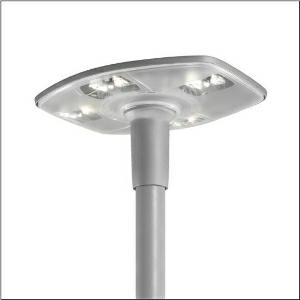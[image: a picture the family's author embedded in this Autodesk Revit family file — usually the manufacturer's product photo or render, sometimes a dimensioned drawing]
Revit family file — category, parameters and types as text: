
# Revit family: dl_r__30_led___st1_2c_5xa513271b08a5_992b
name_source: partatom
category: Lighting Fixtures
units: mm (PartAtom-declared; Revit-internal decimal feet)

## family parameters
Cut with Voids When Loaded = No
Host = Face
Light Source = No
Part Type = Normal
Room Calculation Point = No
Round Connector Dimension = Use Diameter
Shared = No

## types (1)
- --- (1 x LED, 5540 lm, 48.9 W, 4000K)
    Apparent Load = 49 VA
    CIE Flux Codes = 32 71 98 100 100
    Color Rendering = 70
    Color Temperature = 4000K
    Default Elevation = 1800 mm
    Description = DL® 30 LED, mast luminaire, primary light control with 3 zone facetted reflector, of plastic, aluminium vaporised, highly specular, primary optical cover: cover, of PMMA, structured, transparent, light distribution: ST1.2c, light emission: direct distribution, primary light characteristic: asymmetric, crossroads, installation type: post-top, LED High Power LED, rated luminous flux: 5.540 lm, light colour: 740, colour temperature: 4000K, control gear: ECG Plus, control: flexible luminous flux parameterisation, time-dependent luminous flux control, constant luminous flux control, digital communication interface, power reduction, electronic power reduction, mains connection: 220..240V, AC, 50/60Hz, start of lifetime: 49 W, end of lifetime: 51 W, reduction: 23 W, luminaire housing, of diecast aluminium, powder-coated, Siteco® metallic grey (DB 702S), length: 600 mm, width: 510 mm, height: 290mm, spigot size: d x l = 76 x 100mm (post-top) | with reducer (optional accessory) 60 x 100mm, protection rating (complete): IP66, insulation class (complete): insulation class II (safety insulation), certification: CE, ENEC, VDE, impact resistance: IK08, permissible ambient temperature for indoor applications: -25..+30°C, standard-compliant lighting for roads and squares, packaging unit: 1 piece

Light Distribution: ST1.2c
    Height = 290 mm
    Lamp = 1 x LED
    Lamp Light Flux = 5540 lm
    Lamp Power = 48.9 W
    Lamp count = 1
    Length = 510 mm
    Luminous efficacy = 113 lm/W
    Manufacturer = Siteco
    ModVariant = No
    Model = 5XA513271B08A5
    Number of Poles = 1
    OnlyDefault = Yes
    Power Factor = 1
    Product Name = DL® 30 LED | ST1.2c
    Product group = mast luminaire | pylon top
    ProductGroupID = 6100
    Protection Class = Protection class II
    Protection Degree = IP 66
    RLX_Detail_Level = 1
    RlxData = <blob elided: 86577 chars, md5=b1d05cf7>
    Socket = socket
    Standby Power = 0 W
    System Light Flux = 5540 lm
    System Power = 49 W
    Type Comments = factory setting: luminous flux: 100 % | dim-lin: 254 | 497 mA
    Type Image = l_1006003.jpg
    URL = http://relux.com
    VarID = @adj_130929
    Voltage = 0 V
    Weight = 0.00 kg
    Width = 600 mm

## geometry (parser evidence)
native form markers: Blend x4, Sweep x11
no freeform markers — native parametric forms only
